# Revit family: Plumbing_Fixtures_Grohe_Talentofill_Bath_Waste_System_28990000_METRIC
name_source: partatom
category: Pipe Accessories
revit_build: Autodesk Revit 2014 (Build: 20130308_1515(x64)
units: mm (PartAtom-declared; Revit-internal decimal feet)

## types (1)
- Talentofill Pop Up Bath Waste - 28990000
    Adjustable Depth = 43 mm  [stored 0.141076 ft]
    Assembly Code = D20
    AssetType = Fixed
    Body Curve Centre = 34 mm
    Body Radius = 55 mm  [stored 0.180446 ft]
    Body Width = 40 mm  [stored 0.131234 ft]
    ClassificationName = Uniclass2015
    ClassificationValue = Pr_65_54_40_13
    Color = White
    Connection Diameter = 21 mm
    Connection Size Radius = 11 mm
    Description = Talentofill Inlet-, pop-up and waste-system for normal baths with bottle trap and 45°-outlet-bend without finishing trim set 19 952 000 min. recommended pressure 1.0 bar
    DocumentationInstallationGuide = http://cdn08.grohe.com
    DocumentationLiterature = http://cdn08.grohe.com
    DocumentationTechnical = http://cdn08.grohe.com
    Ecojoy = No
    ExpectedLife = 0
    Features = Adjustable waste
    Finish = Metal / Plastic
    Handle Dia = 55 mm  [stored 0.180446 ft]
    Handle Height = 80 mm  [stored 0.262467 ft]
    K Coefficient = 0
    Keynote = S90/620
    Loss Method = K Coefficient
    Manufacturer = Grohe AG
    Material = DR-brass
    Model = Grohe Talentofill Bath Waste - 28990000
    ModelNumber = 29032000
    NBSDescription = Check valves
    NBSObjectName = Check valves
    NBSReference = 90-15-40/323
    Nut Diameter = 38 mm
    Nut Thickness = 13 mm  [stored 0.0426509 ft]
    Plug = Grohe-Chrome
    Product Page Link = http://cdn08.grohe.com
    ProductionYear = 2015
    Spare Parts List = http://cdn08.grohe.com
    TagNumber = Grohe Talentofill Bath Waste - 28990000
    Type Comments = Grohe Talentofill Bath Waste
    TypeName = Grohe Talentofill Bath Waste - 28990000
    URL = http://www.grohe.com
    Valve Material = Grohe - PVC
    WarrantyDurationUnit = Years
    _BIMspec_GUID = 0
    _current revision = 1
    _distributed by = www.bimstore.co.uk

note: [stored X ft] marks values corroborated as IEEE doubles in the binary element streams (Revit-internal decimal feet)

## geometry (parser evidence)
native form markers: Blend x6, Sweep x18
no freeform markers — native parametric forms only
